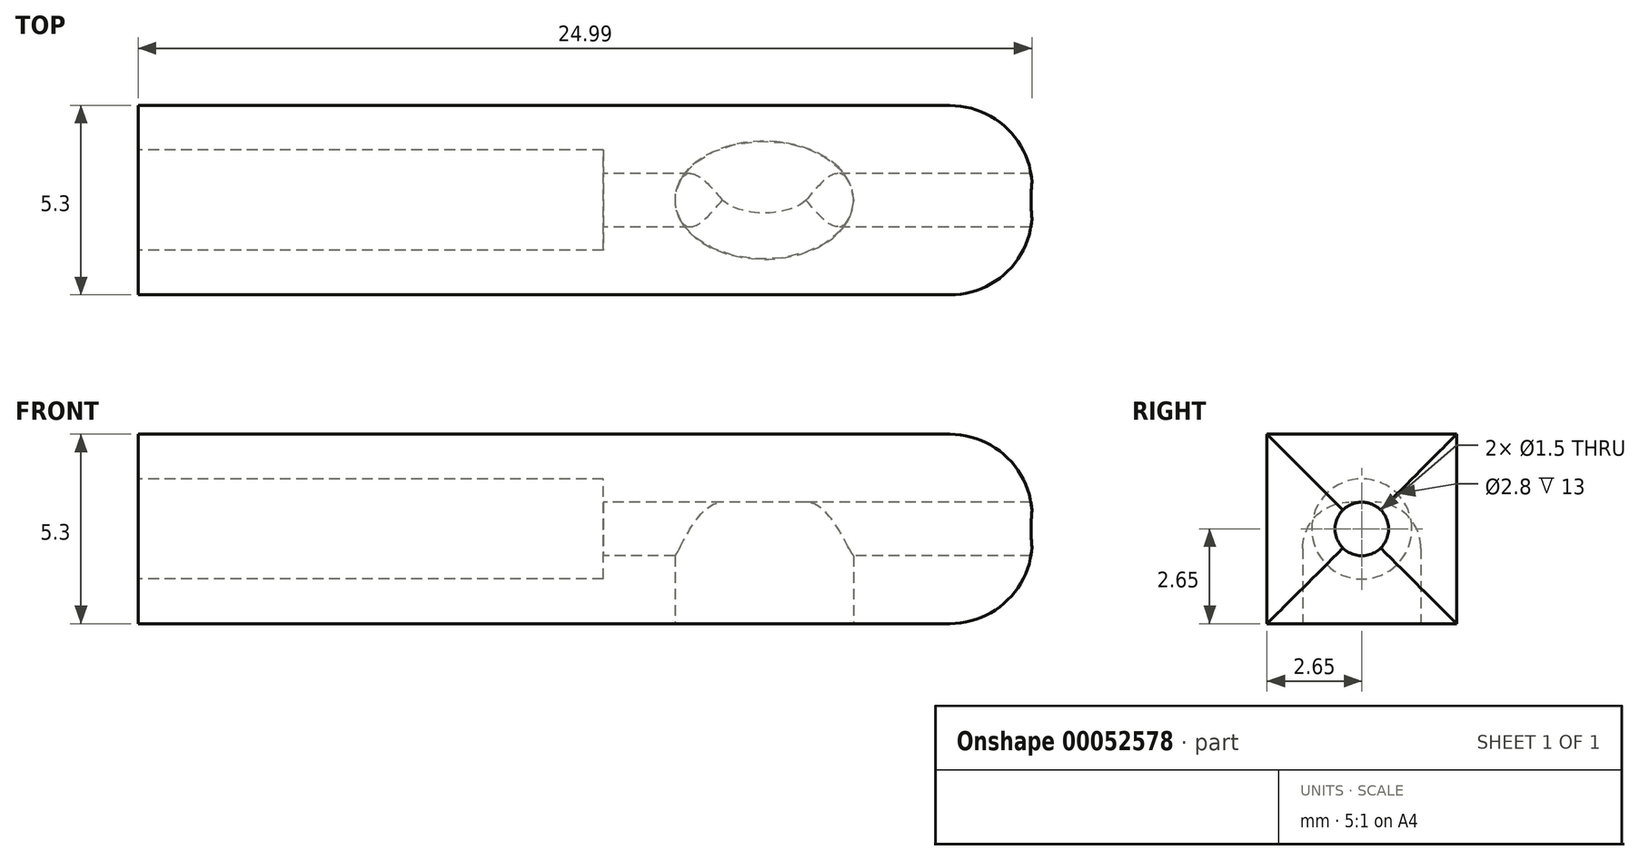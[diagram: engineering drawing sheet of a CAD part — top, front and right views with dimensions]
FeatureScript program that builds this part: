
annotation { "Feature Type Name" : "Feature", "Feature Type Description" : "" }
export const myFeature = defineFeature(function(context is Context, id is Id, definition is map)
    precondition{}
    {
        {
            var Q0;
            Q0=qCreatedBy(makeId("Right.planeOp"),FACE);
            var sketch = newSketch(context, id + "F0", { "sketchPlane" : qUnion([Q0])});
            skLineSegment(sketch, "E0.rect.bottom", {"start": v(2.65, -2.65) * mm, "end": v(-2.65, -2.65) * mm});
            skLineSegment(sketch, "E0.rect.top", {"start": v(2.65, 2.65) * mm, "end": v(-2.65, 2.65) * mm});
            skLineSegment(sketch, "E0.rect.left", {"start": v(2.65, -2.65) * mm, "end": v(2.65, 2.65) * mm});
            skLineSegment(sketch, "E0.rect.right", {"start": v(-2.65, -2.65) * mm, "end": v(-2.65, 2.65) * mm});
            skPoint(sketch, "E0.rect.middle", {"position": v(0, 0) * mm});
            skCircle(sketch, "E1", {"center": v(0, 0) * mm, "radius": 1.4 * mm});
            skCircle(sketch, "E2", {"center": v(0, 0) * mm, "radius": 0.75 * mm});
            skSolve(sketch);
        }
        {
            var Q0;
            Q0=makeQuery(id+"F0.imprint","IMPRINT",FACE,{"disambiguationData":[TD([[makeQuery(id+"F0.imprint","IMPRINT",EDGE,{"derivedFrom":sQuery(id+"F0.wireOp",EDGE,"E0.rect.bottom")}),-1.0]])]});
            var Q1;
            Q1=makeQuery(id+"F0.imprint","IMPRINT",FACE,{"disambiguationData":[TD([[makeQuery(id+"F0.imprint","IMPRINT",EDGE,{"derivedFrom":sQuery(id+"F0.wireOp",EDGE,"E1")}),1.0]])]});
            extrude(context, id + "F1", {"entities" : qUnion([Q0, Q1]), "depth" : 25 * mm});
        }
        {
            var Q0;
            Q0=makeQuery(id+"F0.imprint","IMPRINT",FACE,{"disambiguationData":[TD([[makeQuery(id+"F0.imprint","IMPRINT",EDGE,{"derivedFrom":sQuery(id+"F0.wireOp",EDGE,"E1")}),1.0]])]});
            extrude(context, id + "F2", {"entities" : qUnion([Q0]), "operationType" : NewBodyOperationType.REMOVE, "depth" : 13 * mm});
        }
        {
            var Q0;
            Q0=makeQuery(id+"F1.opExtrude","CAP_EDGE",EDGE,{"disambiguationData":[OSD([sQuery(id+"F0.wireOp",EDGE,"E0.rect.bottom")])],"isStart":false});
            var Q1;
            Q1=makeQuery(id+"F1.opExtrude","CAP_EDGE",EDGE,{"disambiguationData":[OSD([sQuery(id+"F0.wireOp",EDGE,"E0.rect.right")])],"isStart":false});
            var Q2;
            Q2=makeQuery(id+"F1.opExtrude","CAP_EDGE",EDGE,{"disambiguationData":[OSD([sQuery(id+"F0.wireOp",EDGE,"E0.rect.top")])],"isStart":false});
            var Q3;
            Q3=makeQuery(id+"F1.opExtrude","CAP_EDGE",EDGE,{"disambiguationData":[OSD([sQuery(id+"F0.wireOp",EDGE,"E0.rect.left")])],"isStart":false});
            fillet(context, id + "F3", {"entities" : qUnion([Q0, Q1, Q2, Q3]), "radius" : 2.3 * mm, "tangentPropagation" : true, "allowEdgeOverflow" : false});
        }
        {
            var Q0;
            Q0=makeQuery(id+"F1.opExtrude","SWEPT_FACE",FACE,{"disambiguationData":[OSD([sQuery(id+"F0.wireOp",EDGE,"E0.rect.bottom")])]});
            var sketch = newSketch(context, id + "F4", { "sketchPlane" : qUnion([Q0])});
            skEllipse(sketch, "E3", {"center": v(17.5, 0) * mm, "majorRadius": 2.5 * mm, "minorRadius": 1.65 * mm, "majorAxis": v(1, 0)});
            skSolve(sketch);
        }
        {
            var Q0;
            Q0=makeQuery(id+"F4.imprint","IMPRINT",FACE,{"disambiguationData":[TD([[makeQuery(id+"F4.imprint","IMPRINT",EDGE,{"derivedFrom":sQuery(id+"F4.wireOp",EDGE,"E3")}),1.0]])]});
            extrude(context, id + "F5", {"entities" : qUnion([Q0]), "operationType" : NewBodyOperationType.REMOVE, "oppositeDirection" : true, "depth" : 3.4 * mm});
        }
        {
            var Q0;
            Q0=makeQuery(id+"F5.boolean.opBoolean","COPY",EDGE,{"disambiguationData":[OD(0.0)],"derivedFrom":makeQuery(id+"F5.opExtrude","CAP_EDGE",EDGE,{"disambiguationData":[OSD([sQuery(id+"F4.wireOp",EDGE,"E3")])],"isStart":false})});
            var Q1;
            Q1=makeQuery(id+"F5.boolean.opBoolean","COPY",EDGE,{"disambiguationData":[OD(1.0)],"derivedFrom":makeQuery(id+"F5.opExtrude","CAP_EDGE",EDGE,{"disambiguationData":[OSD([sQuery(id+"F4.wireOp",EDGE,"E3")])],"isStart":false})});
            fillet(context, id + "F6", {"entities" : qUnion([Q0, Q1]), "radius" : 1.29 * mm, "tangentPropagation" : true, "allowEdgeOverflow" : false});
        }
    });
